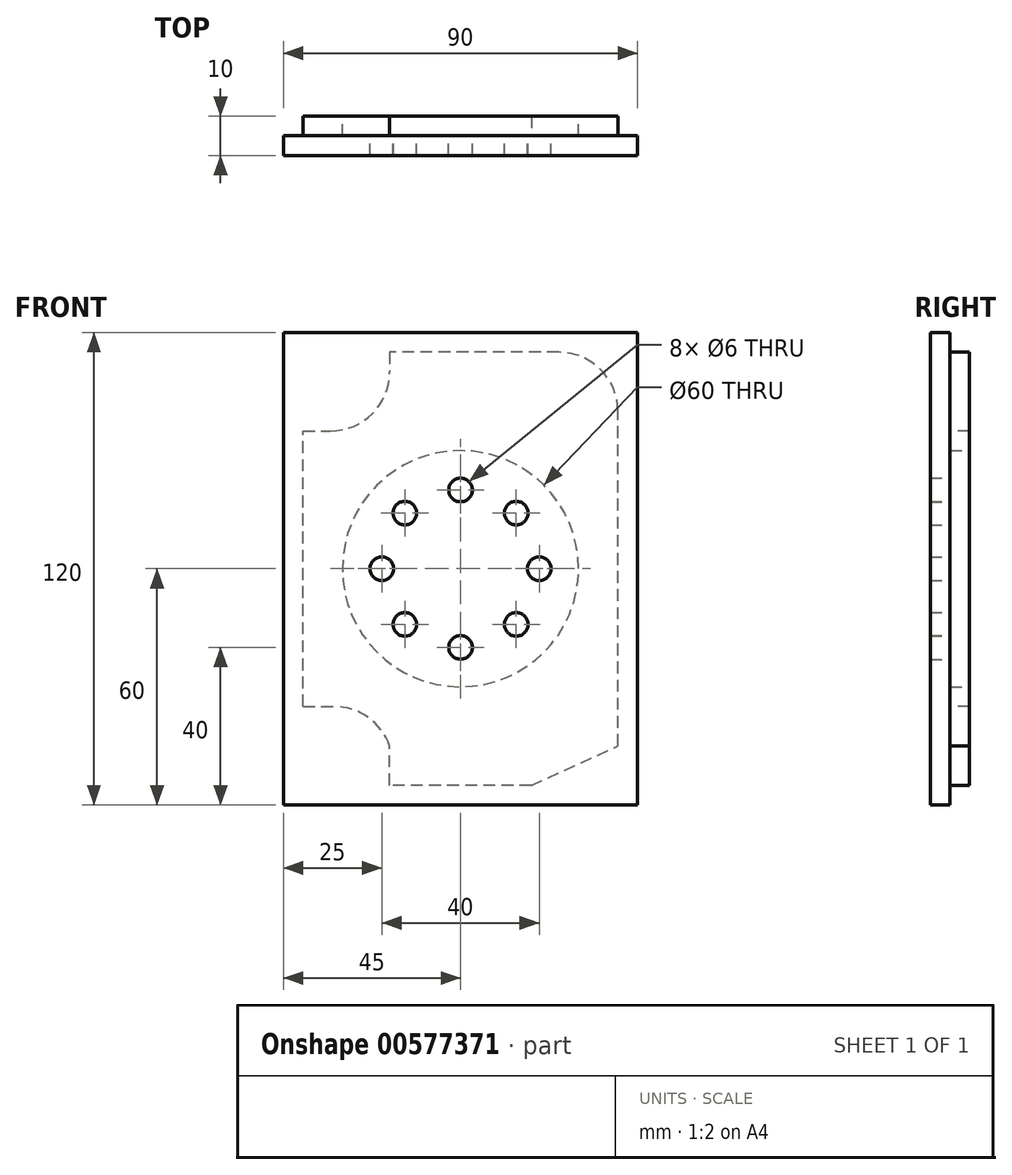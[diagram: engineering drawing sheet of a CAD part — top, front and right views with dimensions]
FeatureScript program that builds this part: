
annotation { "Feature Type Name" : "Feature", "Feature Type Description" : "" }
export const myFeature = defineFeature(function(context is Context, id is Id, definition is map)
    precondition{}
    {
        {
            var Q0;
            Q0=qCreatedBy(makeId("Front.planeOp"),FACE);
            var sketch = newSketch(context, id + "F0", { "sketchPlane" : qUnion([Q0])});
            skLineSegment(sketch, "E0", {"start": v(-45, 60) * mm, "end": v(45, 60) * mm});
            skLineSegment(sketch, "E1", {"start": v(45, 60) * mm, "end": v(45, -60) * mm});
            skLineSegment(sketch, "E2", {"start": v(-45, 0) * mm, "end": v(45, 0) * mm, "construction": true});
            skLineSegment(sketch, "E3", {"start": v(0, -60) * mm, "end": v(0, 60) * mm, "construction": true});
            skPoint(sketch, "E4", {"position": v(0, 0) * mm});
            skLineSegment(sketch, "E5", {"start": v(45, -60) * mm, "end": v(0, -60) * mm});
            skLineSegment(sketch, "E6", {"start": v(-45, 0) * mm, "end": v(-45, 60) * mm});
            skLineSegment(sketch, "E7", {"start": v(0, -60) * mm, "end": v(-45, -60) * mm});
            skLineSegment(sketch, "E8", {"start": v(-45, -60) * mm, "end": v(-45, 0) * mm});
            skSolve(sketch);
        }
        {
            var Q0;
            Q0=makeQuery(id+"F0.imprint","IMPRINT",FACE,{"disambiguationData":[TD([[makeQuery(id+"F0.imprint","IMPRINT",EDGE,{"derivedFrom":sQuery(id+"F0.wireOp",EDGE,"fCPGm3o9-B9AL-qWSV-PlEa-iPMmXyNZCGqo")}),-1.0]])]});
            var Q1;
            Q1=makeQuery(id+"F0.imprint","IMPRINT",FACE,{"disambiguationData":[TD([[makeQuery(id+"F0.imprint","IMPRINT",EDGE,{"derivedFrom":sQuery(id+"F0.wireOp",EDGE,"E0")}),-1.0]])]});
            extrude(context, id + "F1", {"entities" : qUnion([Q0, Q1]), "depth" : 5 * mm, "offsetDistance" : 25 * mm});
        }
        {
            var Q0;
            Q0=makeQuery(id+"F1.opExtrude","CAP_FACE",FACE,{"disambiguationData":[OSD([sQuery(id+"F0.wireOp",EDGE,"fCPGm3o9-B9AL-qWSV-PlEa-iPMmXyNZCGqo"),sQuery(id+"F0.wireOp",EDGE,"E0"),sQuery(id+"F0.wireOp",EDGE,"E1"),sQuery(id+"F0.wireOp",EDGE,"Uf7DkyAE-VfDP-ICNl-ip7P-vBlbmZwNP5hb")])],"isStart":true});
            var sketch = newSketch(context, id + "F2", { "sketchPlane" : qUnion([Q0])});
            skLineSegment(sketch, "E9", {"start": v(-18, -55) * mm, "end": v(18, -55) * mm});
            skLineSegment(sketch, "E10", {"start": v(-18, -55) * mm, "end": v(-40, -45) * mm});
            skLineSegment(sketch, "E11", {"start": v(-40, -45) * mm, "end": v(-40, 40) * mm});
            skLineSegment(sketch, "E12", {"start": v(-25, 55) * mm, "end": v(18, 55) * mm});
            skLineSegment(sketch, "E13", {"start": v(40, -35) * mm, "end": v(40, 35) * mm});
            skLineSegment(sketch, "E14", {"start": v(18, -55) * mm, "end": v(18, -45) * mm});
            skLineSegment(sketch, "E15", {"start": v(40, -35) * mm, "end": v(32.14, -35) * mm});
            skArc(sketch, "E16", {"start": v(32.14, -35) * mm, "mid": v(23.48, -37.75) * mm, "end": v(18, -45) * mm});
            skLineSegment(sketch, "E17", {"start": v(40, 35) * mm, "end": v(33, 35) * mm});
            skLineSegment(sketch, "E18", {"start": v(18, 55) * mm, "end": v(18, 50) * mm});
            skArc(sketch, "E19", {"start": v(18, 50) * mm, "mid": v(22.4, 39.4) * mm, "end": v(33, 35) * mm});
            skArc(sketch, "E20", {"start": v(-25, 55) * mm, "mid": v(-35.6, 50.6) * mm, "end": v(-40, 40) * mm});
            skSolve(sketch);
        }
        {
            var Q0;
            Q0=makeQuery(id+"F2.imprint","IMPRINT",FACE,{"disambiguationData":[TD([[makeQuery(id+"F2.imprint","IMPRINT",EDGE,{"derivedFrom":sQuery(id+"F2.wireOp",EDGE,"E9")}),1.0]])]});
            extrude(context, id + "F3", {"entities" : qUnion([Q0]), "depth" : 5 * mm, "offsetDistance" : 25 * mm});
        }
        {
            var Q0;
            Q0=makeQuery(id+"F3.opExtrude","CAP_FACE",FACE,{"disambiguationData":[OSD([sQuery(id+"F2.wireOp",EDGE,"E9"),sQuery(id+"F2.wireOp",EDGE,"E10"),sQuery(id+"F2.wireOp",EDGE,"E11"),sQuery(id+"F2.wireOp",EDGE,"E12"),sQuery(id+"F2.wireOp",EDGE,"E13"),sQuery(id+"F2.wireOp",EDGE,"E14"),sQuery(id+"F2.wireOp",EDGE,"E15"),sQuery(id+"F2.wireOp",EDGE,"E16"),sQuery(id+"F2.wireOp",EDGE,"E17"),sQuery(id+"F2.wireOp",EDGE,"E18"),sQuery(id+"F2.wireOp",EDGE,"E19"),sQuery(id+"F2.wireOp",EDGE,"E20")])],"isStart":false});
            var sketch = newSketch(context, id + "F4", { "sketchPlane" : qUnion([Q0])});
            skLineSegment(sketch, "E21", {"start": v(0, 0) * mm, "end": v(-89.1, 0) * mm, "construction": true});
            skLineSegment(sketch, "E22", {"start": v(0, 0) * mm, "end": v(0, 119.78) * mm, "construction": true});
            skCircle(sketch, "E23", {"center": v(0, 0) * mm, "radius": 20 * mm});
            skCircle(sketch, "E24", {"center": v(0, -20) * mm, "radius": 3 * mm});
            skCircle(sketch, "E25", {"center": v(-20, 0) * mm, "radius": 3 * mm});
            skCircle(sketch, "E26", {"center": v(0, 20) * mm, "radius": 3 * mm});
            skCircle(sketch, "E27", {"center": v(20, 0) * mm, "radius": 3 * mm});
            skCircle(sketch, "E28", {"center": v(0, 0) * mm, "radius": 30 * mm});
            skCircle(sketch, "E29", {"center": v(-14.14, -14.14) * mm, "radius": 3 * mm});
            skCircle(sketch, "E30", {"center": v(-14.14, 14.14) * mm, "radius": 3 * mm});
            skCircle(sketch, "E31", {"center": v(14.14, 14.14) * mm, "radius": 3 * mm});
            skCircle(sketch, "E32", {"center": v(14.14, -14.14) * mm, "radius": 3 * mm});
            skSolve(sketch);
        }
        {
            var Q0;
            Q0=makeQuery(id+"F4.imprint","IMPRINT",FACE,{"disambiguationData":[TD([[makeQuery(id+"F4.imprint","IMPRINT",EDGE,{"derivedFrom":sQuery(id+"F4.wireOp",EDGE,"E28")}),1.0]])]});
            var Q1;
            {var subQ1=sQuery(id+"F4.wireOp",EDGE,"E23");var subQ15=sQuery(id+"F4.wireOp",EDGE,"E31");var subQ16=makeQuery(id+"F4.imprint","INTERSECT",VERTEX,{"disambiguationData":[OD(0.0)],"derivedFrom":[subQ1,subQ15]});Q1=makeQuery(id+"F4.imprint","IMPRINT",FACE,{"disambiguationData":[TD([[makeQuery(id+"F4.imprint","IMPRINT",EDGE,{"disambiguationData":[TD([[subQ16,1.0]])],"derivedFrom":subQ1}),1.0]])]});}
            extrude(context, id + "F5", {"entities" : qUnion([Q0, Q1]), "operationType" : NewBodyOperationType.REMOVE, "oppositeDirection" : true, "depth" : 5 * mm, "offsetDistance" : 25 * mm});
        }
        {
            var Q0;
            Q0=makeQuery(id+"F5.boolean.opBoolean","SPLIT",FACE,{"disambiguationData":[TD([makeQuery(id+"F5.opExtrude","SWEPT_FACE",FACE,{"disambiguationData":[OSD([sQuery(id+"F4.wireOp",EDGE,"E29")])]})])],"derivedFrom":makeQuery(id+"F3.opExtrude","CAP_FACE",FACE,{"disambiguationData":[OSD([sQuery(id+"F2.wireOp",EDGE,"E9"),sQuery(id+"F2.wireOp",EDGE,"E10"),sQuery(id+"F2.wireOp",EDGE,"E11"),sQuery(id+"F2.wireOp",EDGE,"E12"),sQuery(id+"F2.wireOp",EDGE,"E13"),sQuery(id+"F2.wireOp",EDGE,"E14"),sQuery(id+"F2.wireOp",EDGE,"E15"),sQuery(id+"F2.wireOp",EDGE,"E16"),sQuery(id+"F2.wireOp",EDGE,"E17"),sQuery(id+"F2.wireOp",EDGE,"E18"),sQuery(id+"F2.wireOp",EDGE,"E19"),sQuery(id+"F2.wireOp",EDGE,"E20")])],"isStart":false})});
            var Q1;
            Q1=makeQuery(id+"F5.boolean.opBoolean","SPLIT",FACE,{"disambiguationData":[TD([makeQuery(id+"F5.opExtrude","SWEPT_FACE",FACE,{"disambiguationData":[OSD([sQuery(id+"F4.wireOp",EDGE,"E25")])]})])],"derivedFrom":makeQuery(id+"F3.opExtrude","CAP_FACE",FACE,{"disambiguationData":[OSD([sQuery(id+"F2.wireOp",EDGE,"E9"),sQuery(id+"F2.wireOp",EDGE,"E10"),sQuery(id+"F2.wireOp",EDGE,"E11"),sQuery(id+"F2.wireOp",EDGE,"E12"),sQuery(id+"F2.wireOp",EDGE,"E13"),sQuery(id+"F2.wireOp",EDGE,"E14"),sQuery(id+"F2.wireOp",EDGE,"E15"),sQuery(id+"F2.wireOp",EDGE,"E16"),sQuery(id+"F2.wireOp",EDGE,"E17"),sQuery(id+"F2.wireOp",EDGE,"E18"),sQuery(id+"F2.wireOp",EDGE,"E19"),sQuery(id+"F2.wireOp",EDGE,"E20")])],"isStart":false})});
            var Q2;
            Q2=makeQuery(id+"F5.boolean.opBoolean","SPLIT",FACE,{"disambiguationData":[TD([makeQuery(id+"F5.opExtrude","SWEPT_FACE",FACE,{"disambiguationData":[OSD([sQuery(id+"F4.wireOp",EDGE,"E26")])]})])],"derivedFrom":makeQuery(id+"F3.opExtrude","CAP_FACE",FACE,{"disambiguationData":[OSD([sQuery(id+"F2.wireOp",EDGE,"E9"),sQuery(id+"F2.wireOp",EDGE,"E10"),sQuery(id+"F2.wireOp",EDGE,"E11"),sQuery(id+"F2.wireOp",EDGE,"E12"),sQuery(id+"F2.wireOp",EDGE,"E13"),sQuery(id+"F2.wireOp",EDGE,"E14"),sQuery(id+"F2.wireOp",EDGE,"E15"),sQuery(id+"F2.wireOp",EDGE,"E16"),sQuery(id+"F2.wireOp",EDGE,"E17"),sQuery(id+"F2.wireOp",EDGE,"E18"),sQuery(id+"F2.wireOp",EDGE,"E19"),sQuery(id+"F2.wireOp",EDGE,"E20")])],"isStart":false})});
            var Q3;
            Q3=makeQuery(id+"F5.boolean.opBoolean","SPLIT",FACE,{"disambiguationData":[TD([makeQuery(id+"F5.opExtrude","SWEPT_FACE",FACE,{"disambiguationData":[OSD([sQuery(id+"F4.wireOp",EDGE,"E30")])]})])],"derivedFrom":makeQuery(id+"F3.opExtrude","CAP_FACE",FACE,{"disambiguationData":[OSD([sQuery(id+"F2.wireOp",EDGE,"E9"),sQuery(id+"F2.wireOp",EDGE,"E10"),sQuery(id+"F2.wireOp",EDGE,"E11"),sQuery(id+"F2.wireOp",EDGE,"E12"),sQuery(id+"F2.wireOp",EDGE,"E13"),sQuery(id+"F2.wireOp",EDGE,"E14"),sQuery(id+"F2.wireOp",EDGE,"E15"),sQuery(id+"F2.wireOp",EDGE,"E16"),sQuery(id+"F2.wireOp",EDGE,"E17"),sQuery(id+"F2.wireOp",EDGE,"E18"),sQuery(id+"F2.wireOp",EDGE,"E19"),sQuery(id+"F2.wireOp",EDGE,"E20")])],"isStart":false})});
            var Q4;
            Q4=makeQuery(id+"F5.boolean.opBoolean","SPLIT",FACE,{"disambiguationData":[TD([makeQuery(id+"F5.opExtrude","SWEPT_FACE",FACE,{"disambiguationData":[OSD([sQuery(id+"F4.wireOp",EDGE,"E31")])]})])],"derivedFrom":makeQuery(id+"F3.opExtrude","CAP_FACE",FACE,{"disambiguationData":[OSD([sQuery(id+"F2.wireOp",EDGE,"E9"),sQuery(id+"F2.wireOp",EDGE,"E10"),sQuery(id+"F2.wireOp",EDGE,"E11"),sQuery(id+"F2.wireOp",EDGE,"E12"),sQuery(id+"F2.wireOp",EDGE,"E13"),sQuery(id+"F2.wireOp",EDGE,"E14"),sQuery(id+"F2.wireOp",EDGE,"E15"),sQuery(id+"F2.wireOp",EDGE,"E16"),sQuery(id+"F2.wireOp",EDGE,"E17"),sQuery(id+"F2.wireOp",EDGE,"E18"),sQuery(id+"F2.wireOp",EDGE,"E19"),sQuery(id+"F2.wireOp",EDGE,"E20")])],"isStart":false})});
            var Q5;
            Q5=makeQuery(id+"F5.boolean.opBoolean","SPLIT",FACE,{"disambiguationData":[TD([makeQuery(id+"F5.opExtrude","SWEPT_FACE",FACE,{"disambiguationData":[OSD([sQuery(id+"F4.wireOp",EDGE,"E27")])]})])],"derivedFrom":makeQuery(id+"F3.opExtrude","CAP_FACE",FACE,{"disambiguationData":[OSD([sQuery(id+"F2.wireOp",EDGE,"E9"),sQuery(id+"F2.wireOp",EDGE,"E10"),sQuery(id+"F2.wireOp",EDGE,"E11"),sQuery(id+"F2.wireOp",EDGE,"E12"),sQuery(id+"F2.wireOp",EDGE,"E13"),sQuery(id+"F2.wireOp",EDGE,"E14"),sQuery(id+"F2.wireOp",EDGE,"E15"),sQuery(id+"F2.wireOp",EDGE,"E16"),sQuery(id+"F2.wireOp",EDGE,"E17"),sQuery(id+"F2.wireOp",EDGE,"E18"),sQuery(id+"F2.wireOp",EDGE,"E19"),sQuery(id+"F2.wireOp",EDGE,"E20")])],"isStart":false})});
            var Q6;
            Q6=makeQuery(id+"F5.boolean.opBoolean","SPLIT",FACE,{"disambiguationData":[TD([makeQuery(id+"F5.opExtrude","SWEPT_FACE",FACE,{"disambiguationData":[OSD([sQuery(id+"F4.wireOp",EDGE,"E32")])]})])],"derivedFrom":makeQuery(id+"F3.opExtrude","CAP_FACE",FACE,{"disambiguationData":[OSD([sQuery(id+"F2.wireOp",EDGE,"E9"),sQuery(id+"F2.wireOp",EDGE,"E10"),sQuery(id+"F2.wireOp",EDGE,"E11"),sQuery(id+"F2.wireOp",EDGE,"E12"),sQuery(id+"F2.wireOp",EDGE,"E13"),sQuery(id+"F2.wireOp",EDGE,"E14"),sQuery(id+"F2.wireOp",EDGE,"E15"),sQuery(id+"F2.wireOp",EDGE,"E16"),sQuery(id+"F2.wireOp",EDGE,"E17"),sQuery(id+"F2.wireOp",EDGE,"E18"),sQuery(id+"F2.wireOp",EDGE,"E19"),sQuery(id+"F2.wireOp",EDGE,"E20")])],"isStart":false})});
            var Q7;
            Q7=makeQuery(id+"F5.boolean.opBoolean","SPLIT",FACE,{"disambiguationData":[TD([makeQuery(id+"F5.opExtrude","SWEPT_FACE",FACE,{"disambiguationData":[OSD([sQuery(id+"F4.wireOp",EDGE,"E24")])]})])],"derivedFrom":makeQuery(id+"F3.opExtrude","CAP_FACE",FACE,{"disambiguationData":[OSD([sQuery(id+"F2.wireOp",EDGE,"E9"),sQuery(id+"F2.wireOp",EDGE,"E10"),sQuery(id+"F2.wireOp",EDGE,"E11"),sQuery(id+"F2.wireOp",EDGE,"E12"),sQuery(id+"F2.wireOp",EDGE,"E13"),sQuery(id+"F2.wireOp",EDGE,"E14"),sQuery(id+"F2.wireOp",EDGE,"E15"),sQuery(id+"F2.wireOp",EDGE,"E16"),sQuery(id+"F2.wireOp",EDGE,"E17"),sQuery(id+"F2.wireOp",EDGE,"E18"),sQuery(id+"F2.wireOp",EDGE,"E19"),sQuery(id+"F2.wireOp",EDGE,"E20")])],"isStart":false})});
            extrude(context, id + "F6", {"entities" : qUnion([Q0, Q1, Q2, Q3, Q4, Q5, Q6, Q7]), "operationType" : NewBodyOperationType.REMOVE, "oppositeDirection" : true, "depth" : 10 * mm, "offsetDistance" : 25 * mm});
        }
    });
